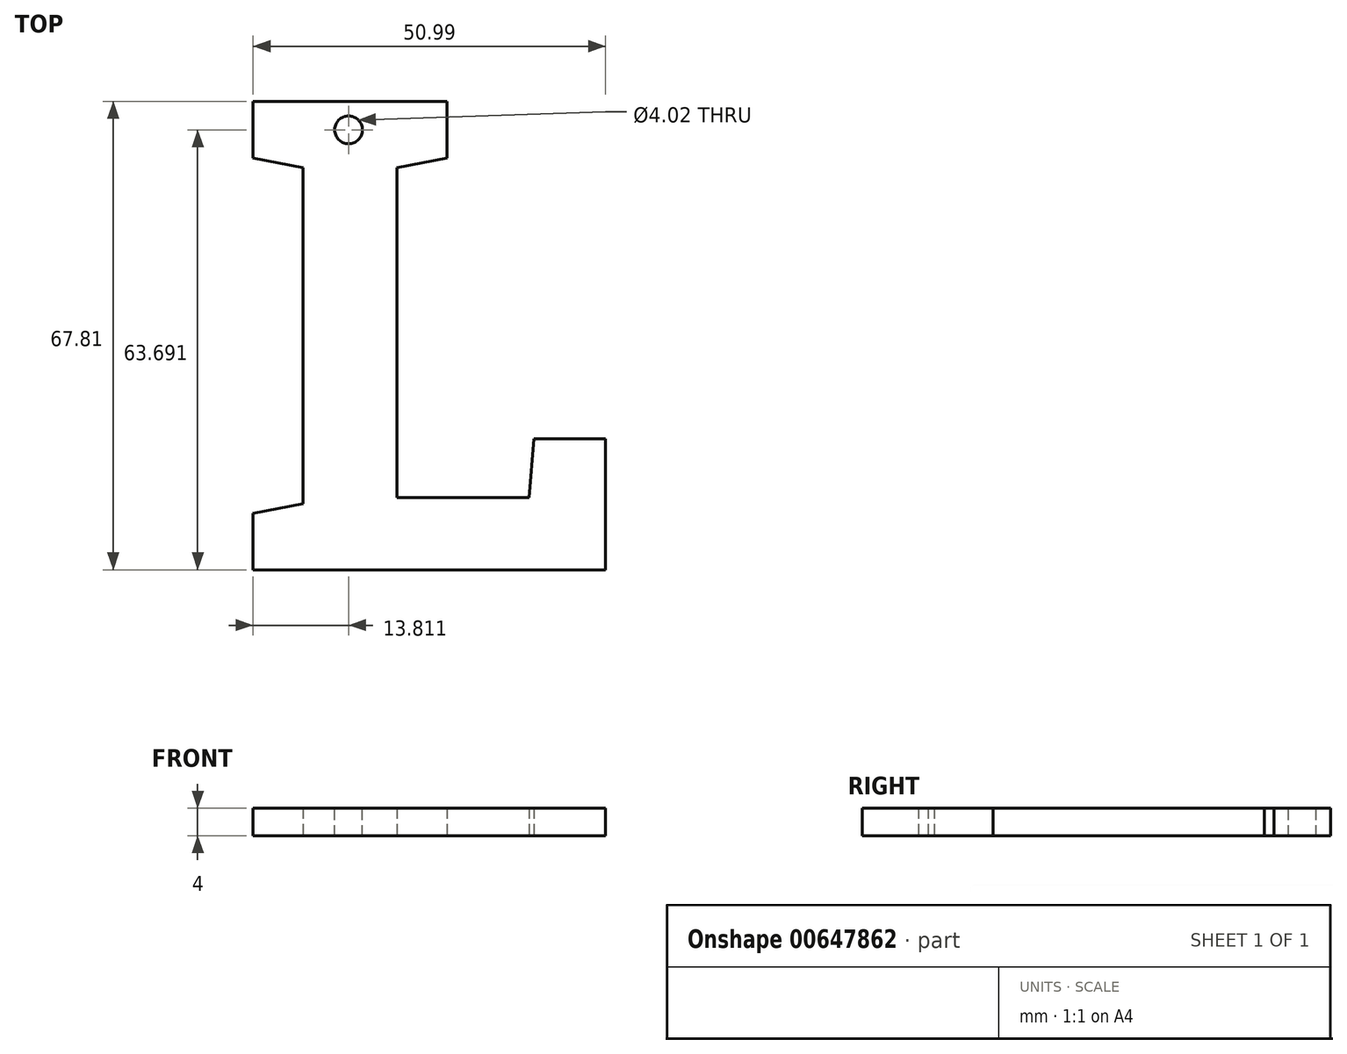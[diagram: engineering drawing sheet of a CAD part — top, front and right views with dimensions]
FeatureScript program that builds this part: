
annotation { "Feature Type Name" : "Feature", "Feature Type Description" : "" }
export const myFeature = defineFeature(function(context is Context, id is Id, definition is map)
    precondition{}
    {
        {
            var Q0;
            Q0=qCreatedBy(makeId("Top.planeOp"),FACE);
            var sketch = newSketch(context, id + "F0", { "sketchPlane" : qUnion([Q0])});
            skText(sketch, "E0", { "text": "L", "fontName": "RobotoSlab-Bold.ttf"});
            const initialGuessF0  = {"E0": [-0.03036, -0.02373, 1, 0, 0.06867]};
            skSetInitialGuess(sketch, initialGuessF0);
            skSolve(sketch);
        }
        {
            var Q0;
            Q0=makeQuery(id+"F0.imprint","IMPRINT",FACE,{"disambiguationData":[TD([[makeQuery(id+"F0.imprint","IMPRINT",EDGE,{"derivedFrom":sQuery(id+"F0.wireOp",EDGE,"E0.sketch_text.stroke-0")}),-1.0]])]});
            extrude(context, id + "F1", {"entities" : qUnion([Q0]), "depth" : 4 * mm, "offsetDistance" : 25 * mm});
        }
        {
            var Q0;
            Q0=makeQuery(id+"F1.opExtrude","CAP_FACE",FACE,{"disambiguationData":[OSD([sQuery(id+"F0.wireOp",EDGE,"E0.sketch_text.stroke-0"),sQuery(id+"F0.wireOp",EDGE,"E0.sketch_text.stroke-1"),sQuery(id+"F0.wireOp",EDGE,"E0.sketch_text.stroke-2"),sQuery(id+"F0.wireOp",EDGE,"E0.sketch_text.stroke-3"),sQuery(id+"F0.wireOp",EDGE,"E0.sketch_text.stroke-4"),sQuery(id+"F0.wireOp",EDGE,"E0.sketch_text.stroke-5"),sQuery(id+"F0.wireOp",EDGE,"E0.sketch_text.stroke-6"),sQuery(id+"F0.wireOp",EDGE,"E0.sketch_text.stroke-7"),sQuery(id+"F0.wireOp",EDGE,"E0.sketch_text.stroke-8"),sQuery(id+"F0.wireOp",EDGE,"E0.sketch_text.stroke-9"),sQuery(id+"F0.wireOp",EDGE,"E0.sketch_text.stroke-10"),sQuery(id+"F0.wireOp",EDGE,"E0.sketch_text.stroke-11"),sQuery(id+"F0.wireOp",EDGE,"E0.sketch_text.stroke-12"),sQuery(id+"F0.wireOp",EDGE,"E0.sketch_text.stroke-13"),sQuery(id+"F0.wireOp",EDGE,"E0.sketch_text.stroke-14"),sQuery(id+"F0.wireOp",EDGE,"E0.sketch_text.stroke-15")])],"isStart":false});
            var sketch = newSketch(context, id + "F2", { "sketchPlane" : qUnion([Q0])});
            skCircle(sketch, "E1", {"center": v(-13.94, 39.96) * mm, "radius": 2 * mm});
            skSolve(sketch);
        }
        {
            var Q0;
            Q0 = qSketchRegion(id + "F2", true);
            extrude(context, id + "F3", {"entities" : qUnion([Q0]), "operationType" : NewBodyOperationType.REMOVE, "endBound" : BoundingType.THROUGH_ALL, "oppositeDirection" : true, "depth" : 25 * mm, "offsetDistance" : 25 * mm});
        }
        {
            var Q0;
            Q0 = qSketchRegion(id + "F2", true);
            extrude(context, id + "F4", {"entities" : qUnion([Q0]), "operationType" : NewBodyOperationType.REMOVE, "endBound" : BoundingType.THROUGH_ALL, "oppositeDirection" : true, "depth" : 25 * mm, "offsetDistance" : 25 * mm});
        }
    });
